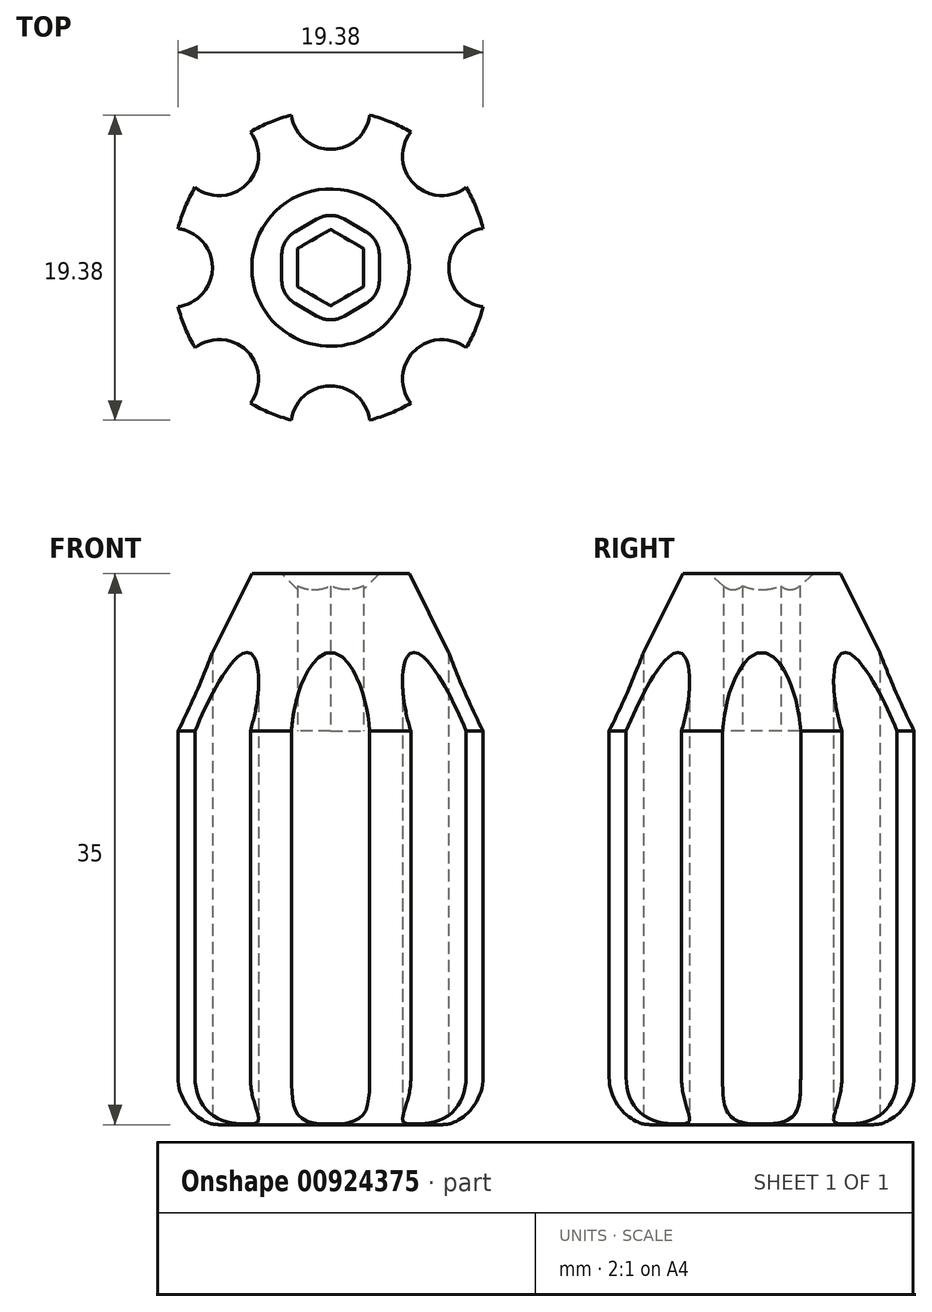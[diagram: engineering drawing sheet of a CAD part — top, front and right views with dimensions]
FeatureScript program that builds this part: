
annotation { "Feature Type Name" : "Feature", "Feature Type Description" : "" }
export const myFeature = defineFeature(function(context is Context, id is Id, definition is map)
    precondition{}
    {
        {
            var Q0;
            Q0=qCreatedBy(makeId("Top.planeOp"),FACE);
            var sketch = newSketch(context, id + "F0", { "sketchPlane" : qUnion([Q0])});
            skCircle(sketch, "E0", {"center": v(0, 0) * mm, "radius": 10 * mm});
            skCircle(sketch, "E1.cCircle", {"center": v(0, 0) * mm, "radius": 2.1 * mm, "construction": true});
            skLineSegment(sketch, "E1.0", {"start": v(2.1, 1.21) * mm, "end": v(2.1, -1.21) * mm});
            skLineSegment(sketch, "E1.1", {"start": v(2.1, -1.21) * mm, "end": v(0, -2.42) * mm});
            skLineSegment(sketch, "E1.2", {"start": v(0, -2.42) * mm, "end": v(-2.1, -1.21) * mm});
            skLineSegment(sketch, "E1.3", {"start": v(-2.1, -1.21) * mm, "end": v(-2.1, 1.21) * mm});
            skLineSegment(sketch, "E1.4", {"start": v(-2.1, 1.21) * mm, "end": v(0, 2.42) * mm});
            skLineSegment(sketch, "E1.5", {"start": v(0, 2.42) * mm, "end": v(2.1, 1.21) * mm});
            skPoint(sketch, "E1.0.midPoint", {"position": v(2.1, 0) * mm});
            skCircle(sketch, "E2", {"center": v(0, 10) * mm, "radius": 2.5 * mm});
            skCircle(sketch, "E3.1.0", {"center": v(-7.07, 7.07) * mm, "radius": 2.5 * mm});
            skCircle(sketch, "E3.2.0", {"center": v(-10, 0) * mm, "radius": 2.5 * mm});
            skCircle(sketch, "E3.3.0", {"center": v(-7.07, -7.07) * mm, "radius": 2.5 * mm});
            skCircle(sketch, "E3.4.0", {"center": v(0, -10) * mm, "radius": 2.5 * mm});
            skCircle(sketch, "E3.5.0", {"center": v(7.07, -7.07) * mm, "radius": 2.5 * mm});
            skCircle(sketch, "E3.6.0", {"center": v(10, 0) * mm, "radius": 2.5 * mm});
            skCircle(sketch, "E3.7.0", {"center": v(7.07, 7.07) * mm, "radius": 2.5 * mm});
            skSolve(sketch);
        }
        {
            var Q0;
            {var subQ6=sQuery(id+"F0.wireOp",EDGE,"E0");var subQ9=sQuery(id+"F0.wireOp",EDGE,"E3.1.0");var subQ10=makeQuery(id+"F0.imprint","INTERSECT",VERTEX,{"disambiguationData":[OD(1.0)],"derivedFrom":[subQ6,subQ9]});Q0=makeQuery(id+"F0.imprint","IMPRINT",FACE,{"disambiguationData":[TD([[makeQuery(id+"F0.imprint","IMPRINT",EDGE,{"disambiguationData":[TD([[subQ10,-1.0]])],"derivedFrom":subQ6}),1.0]])]});}
            var Q1;
            {var subQ0=sQuery(id+"F0.wireOp",EDGE,"Lzq0tQn3-zmQ7-VaXY-TnWL-NvxHLgQxm2Bj");var subQ1=sQuery(id+"F0.wireOp",EDGE,"DYPGsvN2-RAWE-5xOr-ueOZ-kodBmIYwBUKR");var subQ2=makeQuery(id+"F0.imprint","INTERSECT",VERTEX,{"disambiguationData":[OD(0.0)],"derivedFrom":[subQ1,subQ0]});Q1=makeQuery(id+"F0.imprint","IMPRINT",FACE,{"disambiguationData":[TD([[makeQuery(id+"F0.imprint","IMPRINT",EDGE,{"disambiguationData":[TD([[subQ2,-1.0]])],"derivedFrom":subQ1}),1.0]])]});}
            var Q2;
            {var subQ1=sQuery(id+"F0.wireOp",EDGE,"E0");var subQ12=sQuery(id+"F0.wireOp",EDGE,"E3.11.0");var subQ13=makeQuery(id+"F0.imprint","INTERSECT",VERTEX,{"disambiguationData":[OD(1.0)],"derivedFrom":[subQ1,subQ12]});Q2=makeQuery(id+"F0.imprint","IMPRINT",FACE,{"disambiguationData":[TD([[makeQuery(id+"F0.imprint","IMPRINT",EDGE,{"disambiguationData":[TD([[subQ13,-1.0]])],"derivedFrom":subQ1}),1.0]])]});}
            var Q3;
            {var subQ5=sQuery(id+"F0.wireOp",EDGE,"E3.10.0");var subQ6=sQuery(id+"F0.wireOp",EDGE,"E0");var subQ7=makeQuery(id+"F0.imprint","INTERSECT",VERTEX,{"disambiguationData":[OD(1.0)],"derivedFrom":[subQ6,subQ5]});Q3=makeQuery(id+"F0.imprint","IMPRINT",FACE,{"disambiguationData":[TD([[makeQuery(id+"F0.imprint","IMPRINT",EDGE,{"disambiguationData":[TD([[subQ7,-1.0]])],"derivedFrom":subQ6}),1.0]])]});}
            var Q4;
            {var subQ1=sQuery(id+"F0.wireOp",EDGE,"E0");var subQ8=sQuery(id+"F0.wireOp",EDGE,"E3.10.0");var subQ9=makeQuery(id+"F0.imprint","INTERSECT",VERTEX,{"disambiguationData":[OD(0.0)],"derivedFrom":[subQ1,subQ8]});Q4=makeQuery(id+"F0.imprint","IMPRINT",FACE,{"disambiguationData":[TD([[makeQuery(id+"F0.imprint","IMPRINT",EDGE,{"disambiguationData":[TD([[subQ9,1.0]])],"derivedFrom":subQ1}),1.0]])]});}
            var Q5;
            {var subQ0=sQuery(id+"F0.wireOp",EDGE,"iq5nXlA1-twKB-VV0K-wLbr-YbvAK5noPxXK");var subQ1=sQuery(id+"F0.wireOp",EDGE,"E0");var subQ2=makeQuery(id+"F0.imprint","INTERSECT",VERTEX,{"disambiguationData":[OD(1.0)],"derivedFrom":[subQ1,subQ0]});Q5=makeQuery(id+"F0.imprint","IMPRINT",FACE,{"disambiguationData":[TD([[makeQuery(id+"F0.imprint","IMPRINT",EDGE,{"disambiguationData":[TD([[subQ2,-1.0]])],"derivedFrom":subQ1}),1.0]])]});}
            var Q6;
            {var subQ0=sQuery(id+"F0.wireOp",EDGE,"iq5nXlA1-twKB-VV0K-wLbr-YbvAK5noPxXK");var subQ1=sQuery(id+"F0.wireOp",EDGE,"E0");var subQ2=makeQuery(id+"F0.imprint","INTERSECT",VERTEX,{"disambiguationData":[OD(1.0)],"derivedFrom":[subQ1,subQ0]});Q6=makeQuery(id+"F0.imprint","IMPRINT",FACE,{"disambiguationData":[TD([[makeQuery(id+"F0.imprint","IMPRINT",EDGE,{"disambiguationData":[TD([[subQ2,1.0]])],"derivedFrom":subQ1}),1.0]])]});}
            var Q7;
            {var subQ0=sQuery(id+"F0.wireOp",EDGE,"LrOnNZfW-nTIl-rACn-o9rB-nAGoXEMnr8V9");var subQ1=sQuery(id+"F0.wireOp",EDGE,"E0");var subQ2=makeQuery(id+"F0.imprint","INTERSECT",VERTEX,{"disambiguationData":[OD(0.0)],"derivedFrom":[subQ1,subQ0]});Q7=makeQuery(id+"F0.imprint","IMPRINT",FACE,{"disambiguationData":[TD([[makeQuery(id+"F0.imprint","IMPRINT",EDGE,{"disambiguationData":[TD([[subQ2,1.0]])],"derivedFrom":subQ1}),1.0]])]});}
            var Q8;
            {var subQ0=sQuery(id+"F0.wireOp",EDGE,"Lzq0tQn3-zmQ7-VaXY-TnWL-NvxHLgQxm2Bj");var subQ1=sQuery(id+"F0.wireOp",EDGE,"E0");var subQ2=makeQuery(id+"F0.imprint","INTERSECT",VERTEX,{"disambiguationData":[OD(1.0)],"derivedFrom":[subQ1,subQ0]});Q8=makeQuery(id+"F0.imprint","IMPRINT",FACE,{"disambiguationData":[TD([[makeQuery(id+"F0.imprint","IMPRINT",EDGE,{"disambiguationData":[TD([[subQ2,-1.0]])],"derivedFrom":subQ1}),1.0]])]});}
            var Q9;
            {var subQ0=sQuery(id+"F0.wireOp",EDGE,"Lzq0tQn3-zmQ7-VaXY-TnWL-NvxHLgQxm2Bj");var subQ1=sQuery(id+"F0.wireOp",EDGE,"E0");var subQ2=makeQuery(id+"F0.imprint","INTERSECT",VERTEX,{"disambiguationData":[OD(1.0)],"derivedFrom":[subQ1,subQ0]});Q9=makeQuery(id+"F0.imprint","IMPRINT",FACE,{"disambiguationData":[TD([[makeQuery(id+"F0.imprint","IMPRINT",EDGE,{"disambiguationData":[TD([[subQ2,1.0]])],"derivedFrom":subQ1}),1.0]])]});}
            var Q10;
            {var subQ1=sQuery(id+"F0.wireOp",EDGE,"E0");var subQ5=sQuery(id+"F0.wireOp",EDGE,"E3.7.0");var subQ6=makeQuery(id+"F0.imprint","INTERSECT",VERTEX,{"disambiguationData":[OD(1.0)],"derivedFrom":[subQ1,subQ5]});Q10=makeQuery(id+"F0.imprint","IMPRINT",FACE,{"disambiguationData":[TD([[makeQuery(id+"F0.imprint","IMPRINT",EDGE,{"disambiguationData":[TD([[subQ6,-1.0]])],"derivedFrom":subQ1}),1.0]])]});}
            var Q11;
            {var subQ0=sQuery(id+"F0.wireOp",EDGE,"E3.9.0");var subQ1=sQuery(id+"F0.wireOp",EDGE,"E0");var subQ2=makeQuery(id+"F0.imprint","INTERSECT",VERTEX,{"disambiguationData":[OD(0.0)],"derivedFrom":[subQ1,subQ0]});Q11=makeQuery(id+"F0.imprint","IMPRINT",FACE,{"disambiguationData":[TD([[makeQuery(id+"F0.imprint","IMPRINT",EDGE,{"disambiguationData":[TD([[subQ2,1.0]])],"derivedFrom":subQ1}),1.0]])]});}
            var Q12;
            {var subQ0=sQuery(id+"F0.wireOp",EDGE,"E3.5.0");var subQ1=sQuery(id+"F0.wireOp",EDGE,"E0");var subQ2=makeQuery(id+"F0.imprint","INTERSECT",VERTEX,{"disambiguationData":[OD(1.0)],"derivedFrom":[subQ1,subQ0]});Q12=makeQuery(id+"F0.imprint","IMPRINT",FACE,{"disambiguationData":[TD([[makeQuery(id+"F0.imprint","IMPRINT",EDGE,{"disambiguationData":[TD([[subQ2,-1.0]])],"derivedFrom":subQ1}),1.0]])]});}
            var Q13;
            {var subQ0=sQuery(id+"F0.wireOp",EDGE,"E3.6.0");var subQ1=sQuery(id+"F0.wireOp",EDGE,"E0");var subQ2=makeQuery(id+"F0.imprint","INTERSECT",VERTEX,{"disambiguationData":[OD(0.0)],"derivedFrom":[subQ1,subQ0]});Q13=makeQuery(id+"F0.imprint","IMPRINT",FACE,{"disambiguationData":[TD([[makeQuery(id+"F0.imprint","IMPRINT",EDGE,{"disambiguationData":[TD([[subQ2,-1.0]])],"derivedFrom":subQ1}),1.0]])]});}
            var Q14;
            {var subQ0=sQuery(id+"F0.wireOp",EDGE,"DaHCeAtm-5SFQ-LGW9-yzzW-rRFCzOuSfmrK");var subQ1=sQuery(id+"F0.wireOp",EDGE,"E0");var subQ2=makeQuery(id+"F0.imprint","INTERSECT",VERTEX,{"disambiguationData":[OD(0.0)],"derivedFrom":[subQ1,subQ0]});Q14=makeQuery(id+"F0.imprint","IMPRINT",FACE,{"disambiguationData":[TD([[makeQuery(id+"F0.imprint","IMPRINT",EDGE,{"disambiguationData":[TD([[subQ2,-1.0]])],"derivedFrom":subQ1}),1.0]])]});}
            var Q15;
            {var subQ0=sQuery(id+"F0.wireOp",EDGE,"DaHCeAtm-5SFQ-LGW9-yzzW-rRFCzOuSfmrK");var subQ1=sQuery(id+"F0.wireOp",EDGE,"E0");var subQ2=makeQuery(id+"F0.imprint","INTERSECT",VERTEX,{"disambiguationData":[OD(0.0)],"derivedFrom":[subQ1,subQ0]});Q15=makeQuery(id+"F0.imprint","IMPRINT",FACE,{"disambiguationData":[TD([[makeQuery(id+"F0.imprint","IMPRINT",EDGE,{"disambiguationData":[TD([[subQ2,1.0]])],"derivedFrom":subQ1}),1.0]])]});}
            var Q16;
            {var subQ1=sQuery(id+"F0.wireOp",EDGE,"E0");var subQ9=sQuery(id+"F0.wireOp",EDGE,"E3.4.0");var subQ10=makeQuery(id+"F0.imprint","INTERSECT",VERTEX,{"disambiguationData":[OD(1.0)],"derivedFrom":[subQ1,subQ9]});Q16=makeQuery(id+"F0.imprint","IMPRINT",FACE,{"disambiguationData":[TD([[makeQuery(id+"F0.imprint","IMPRINT",EDGE,{"disambiguationData":[TD([[subQ10,-1.0]])],"derivedFrom":subQ1}),1.0]])]});}
            var Q17;
            {var subQ0=sQuery(id+"F0.wireOp",EDGE,"LrOnNZfW-nTIl-rACn-o9rB-nAGoXEMnr8V9");var subQ1=sQuery(id+"F0.wireOp",EDGE,"E0");var subQ2=makeQuery(id+"F0.imprint","INTERSECT",VERTEX,{"disambiguationData":[OD(1.0)],"derivedFrom":[subQ1,subQ0]});Q17=makeQuery(id+"F0.imprint","IMPRINT",FACE,{"disambiguationData":[TD([[makeQuery(id+"F0.imprint","IMPRINT",EDGE,{"disambiguationData":[TD([[subQ2,-1.0]])],"derivedFrom":subQ1}),1.0]])]});}
            var Q18;
            {var subQ0=sQuery(id+"F0.wireOp",EDGE,"LrOnNZfW-nTIl-rACn-o9rB-nAGoXEMnr8V9");var subQ1=sQuery(id+"F0.wireOp",EDGE,"E0");var subQ2=makeQuery(id+"F0.imprint","INTERSECT",VERTEX,{"disambiguationData":[OD(1.0)],"derivedFrom":[subQ1,subQ0]});Q18=makeQuery(id+"F0.imprint","IMPRINT",FACE,{"disambiguationData":[TD([[makeQuery(id+"F0.imprint","IMPRINT",EDGE,{"disambiguationData":[TD([[subQ2,1.0]])],"derivedFrom":subQ1}),1.0]])]});}
            var Q19;
            {var subQ0=sQuery(id+"F0.wireOp",EDGE,"E3.2.0");var subQ1=sQuery(id+"F0.wireOp",EDGE,"E0");var subQ2=makeQuery(id+"F0.imprint","INTERSECT",VERTEX,{"disambiguationData":[OD(1.0)],"derivedFrom":[subQ1,subQ0]});Q19=makeQuery(id+"F0.imprint","IMPRINT",FACE,{"disambiguationData":[TD([[makeQuery(id+"F0.imprint","IMPRINT",EDGE,{"disambiguationData":[TD([[subQ2,-1.0]])],"derivedFrom":subQ1}),1.0]])]});}
            var Q20;
            {var subQ0=sQuery(id+"F0.wireOp",EDGE,"iq5nXlA1-twKB-VV0K-wLbr-YbvAK5noPxXK");var subQ1=sQuery(id+"F0.wireOp",EDGE,"E0");var subQ2=makeQuery(id+"F0.imprint","INTERSECT",VERTEX,{"disambiguationData":[OD(0.0)],"derivedFrom":[subQ1,subQ0]});Q20=makeQuery(id+"F0.imprint","IMPRINT",FACE,{"disambiguationData":[TD([[makeQuery(id+"F0.imprint","IMPRINT",EDGE,{"disambiguationData":[TD([[subQ2,-1.0]])],"derivedFrom":subQ1}),1.0]])]});}
            var Q21;
            {var subQ0=sQuery(id+"F0.wireOp",EDGE,"iq5nXlA1-twKB-VV0K-wLbr-YbvAK5noPxXK");var subQ1=sQuery(id+"F0.wireOp",EDGE,"E0");var subQ2=makeQuery(id+"F0.imprint","INTERSECT",VERTEX,{"disambiguationData":[OD(0.0)],"derivedFrom":[subQ1,subQ0]});Q21=makeQuery(id+"F0.imprint","IMPRINT",FACE,{"disambiguationData":[TD([[makeQuery(id+"F0.imprint","IMPRINT",EDGE,{"disambiguationData":[TD([[subQ2,1.0]])],"derivedFrom":subQ1}),1.0]])]});}
            var Q22;
            {var subQ0=sQuery(id+"F0.wireOp",EDGE,"E2");var subQ1=sQuery(id+"F0.wireOp",EDGE,"E0");var subQ2=makeQuery(id+"F0.imprint","INTERSECT",VERTEX,{"disambiguationData":[OD(0.0)],"derivedFrom":[subQ1,subQ0]});Q22=makeQuery(id+"F0.imprint","IMPRINT",FACE,{"disambiguationData":[TD([[makeQuery(id+"F0.imprint","IMPRINT",EDGE,{"disambiguationData":[TD([[subQ2,-1.0]])],"derivedFrom":subQ1}),1.0]])]});}
            var Q23;
            {var subQ0=sQuery(id+"F0.wireOp",EDGE,"Lzq0tQn3-zmQ7-VaXY-TnWL-NvxHLgQxm2Bj");var subQ1=sQuery(id+"F0.wireOp",EDGE,"E0");var subQ2=makeQuery(id+"F0.imprint","INTERSECT",VERTEX,{"disambiguationData":[OD(0.0)],"derivedFrom":[subQ1,subQ0]});Q23=makeQuery(id+"F0.imprint","IMPRINT",FACE,{"disambiguationData":[TD([[makeQuery(id+"F0.imprint","IMPRINT",EDGE,{"disambiguationData":[TD([[subQ2,-1.0]])],"derivedFrom":subQ1}),1.0]])]});}
            var Q24;
            {var subQ0=sQuery(id+"F0.wireOp",EDGE,"Lzq0tQn3-zmQ7-VaXY-TnWL-NvxHLgQxm2Bj");var subQ1=sQuery(id+"F0.wireOp",EDGE,"E0");var subQ2=makeQuery(id+"F0.imprint","INTERSECT",VERTEX,{"disambiguationData":[OD(0.0)],"derivedFrom":[subQ1,subQ0]});Q24=makeQuery(id+"F0.imprint","IMPRINT",FACE,{"disambiguationData":[TD([[makeQuery(id+"F0.imprint","IMPRINT",EDGE,{"disambiguationData":[TD([[subQ2,1.0]])],"derivedFrom":subQ1}),1.0]])]});}
            var Q25;
            {var subQ0=sQuery(id+"F0.wireOp",EDGE,"LrOnNZfW-nTIl-rACn-o9rB-nAGoXEMnr8V9");var subQ1=sQuery(id+"F0.wireOp",EDGE,"E0");var subQ2=makeQuery(id+"F0.imprint","INTERSECT",VERTEX,{"disambiguationData":[OD(0.0)],"derivedFrom":[subQ1,subQ0]});Q25=makeQuery(id+"F0.imprint","IMPRINT",FACE,{"disambiguationData":[TD([[makeQuery(id+"F0.imprint","IMPRINT",EDGE,{"disambiguationData":[TD([[subQ2,-1.0]])],"derivedFrom":subQ1}),1.0]])]});}
            var Q26;
            {var subQ0=sQuery(id+"F0.wireOp",EDGE,"DaHCeAtm-5SFQ-LGW9-yzzW-rRFCzOuSfmrK");var subQ1=sQuery(id+"F0.wireOp",EDGE,"E0");var subQ2=makeQuery(id+"F0.imprint","INTERSECT",VERTEX,{"disambiguationData":[OD(1.0)],"derivedFrom":[subQ1,subQ0]});Q26=makeQuery(id+"F0.imprint","IMPRINT",FACE,{"disambiguationData":[TD([[makeQuery(id+"F0.imprint","IMPRINT",EDGE,{"disambiguationData":[TD([[subQ2,1.0]])],"derivedFrom":subQ1}),1.0]])]});}
            var Q27;
            {var subQ0=sQuery(id+"F0.wireOp",EDGE,"DaHCeAtm-5SFQ-LGW9-yzzW-rRFCzOuSfmrK");var subQ1=sQuery(id+"F0.wireOp",EDGE,"E0");var subQ2=makeQuery(id+"F0.imprint","INTERSECT",VERTEX,{"disambiguationData":[OD(1.0)],"derivedFrom":[subQ1,subQ0]});Q27=makeQuery(id+"F0.imprint","IMPRINT",FACE,{"disambiguationData":[TD([[makeQuery(id+"F0.imprint","IMPRINT",EDGE,{"disambiguationData":[TD([[subQ2,-1.0]])],"derivedFrom":subQ1}),1.0]])]});}
            var Q28;
            {var subQ0=sQuery(id+"F0.wireOp",EDGE,"DaHCeAtm-5SFQ-LGW9-yzzW-rRFCzOuSfmrK");var subQ1=sQuery(id+"F0.wireOp",EDGE,"DYPGsvN2-RAWE-5xOr-ueOZ-kodBmIYwBUKR");var subQ2=makeQuery(id+"F0.imprint","INTERSECT",VERTEX,{"disambiguationData":[OD(1.0)],"derivedFrom":[subQ1,subQ0]});Q28=makeQuery(id+"F0.imprint","IMPRINT",FACE,{"disambiguationData":[TD([[makeQuery(id+"F0.imprint","IMPRINT",EDGE,{"disambiguationData":[TD([[subQ2,-1.0]])],"derivedFrom":subQ1}),1.0]])]});}
            var Q29;
            {var subQ0=sQuery(id+"F0.wireOp",EDGE,"iq5nXlA1-twKB-VV0K-wLbr-YbvAK5noPxXK");var subQ1=sQuery(id+"F0.wireOp",EDGE,"DYPGsvN2-RAWE-5xOr-ueOZ-kodBmIYwBUKR");var subQ2=makeQuery(id+"F0.imprint","INTERSECT",VERTEX,{"disambiguationData":[OD(1.0)],"derivedFrom":[subQ1,subQ0]});Q29=makeQuery(id+"F0.imprint","IMPRINT",FACE,{"disambiguationData":[TD([[makeQuery(id+"F0.imprint","IMPRINT",EDGE,{"disambiguationData":[TD([[subQ2,-1.0]])],"derivedFrom":subQ1}),1.0]])]});}
            var Q30;
            Q30=makeQuery(id+"F0.imprint","IMPRINT",FACE,{"disambiguationData":[TD([[makeQuery(id+"F0.imprint","IMPRINT",EDGE,{"derivedFrom":sQuery(id+"F0.wireOp",EDGE,"E1.0")}),1.0]])]});
            var Q31;
            {var subQ0=sQuery(id+"F0.wireOp",EDGE,"iq5nXlA1-twKB-VV0K-wLbr-YbvAK5noPxXK");var subQ1=sQuery(id+"F0.wireOp",EDGE,"DYPGsvN2-RAWE-5xOr-ueOZ-kodBmIYwBUKR");var subQ2=makeQuery(id+"F0.imprint","INTERSECT",VERTEX,{"disambiguationData":[OD(0.0)],"derivedFrom":[subQ1,subQ0]});Q31=makeQuery(id+"F0.imprint","IMPRINT",FACE,{"disambiguationData":[TD([[makeQuery(id+"F0.imprint","IMPRINT",EDGE,{"disambiguationData":[TD([[subQ2,1.0]])],"derivedFrom":subQ1}),1.0]])]});}
            var Q32;
            {var subQ0=sQuery(id+"F0.wireOp",EDGE,"E3.3.0");var subQ1=sQuery(id+"F0.wireOp",EDGE,"E0");var subQ2=makeQuery(id+"F0.imprint","INTERSECT",VERTEX,{"disambiguationData":[OD(0.0)],"derivedFrom":[subQ1,subQ0]});Q32=makeQuery(id+"F0.imprint","IMPRINT",FACE,{"disambiguationData":[TD([[makeQuery(id+"F0.imprint","IMPRINT",EDGE,{"disambiguationData":[TD([[subQ2,-1.0]])],"derivedFrom":subQ1}),1.0]])]});}
            var Q33;
            {var subQ0=sQuery(id+"F0.wireOp",EDGE,"E3.2.0");var subQ1=sQuery(id+"F0.wireOp",EDGE,"E0");var subQ2=makeQuery(id+"F0.imprint","INTERSECT",VERTEX,{"disambiguationData":[OD(0.0)],"derivedFrom":[subQ1,subQ0]});Q33=makeQuery(id+"F0.imprint","IMPRINT",FACE,{"disambiguationData":[TD([[makeQuery(id+"F0.imprint","IMPRINT",EDGE,{"disambiguationData":[TD([[subQ2,-1.0]])],"derivedFrom":subQ1}),1.0]])]});}
            var Q34;
            {var subQ0=sQuery(id+"F0.wireOp",EDGE,"E3.4.0");var subQ1=sQuery(id+"F0.wireOp",EDGE,"E0");var subQ2=makeQuery(id+"F0.imprint","INTERSECT",VERTEX,{"disambiguationData":[OD(0.0)],"derivedFrom":[subQ1,subQ0]});Q34=makeQuery(id+"F0.imprint","IMPRINT",FACE,{"disambiguationData":[TD([[makeQuery(id+"F0.imprint","IMPRINT",EDGE,{"disambiguationData":[TD([[subQ2,-1.0]])],"derivedFrom":subQ1}),1.0]])]});}
            var Q35;
            {var subQ0=sQuery(id+"F0.wireOp",EDGE,"E3.5.0");var subQ1=sQuery(id+"F0.wireOp",EDGE,"E0");var subQ2=makeQuery(id+"F0.imprint","INTERSECT",VERTEX,{"disambiguationData":[OD(0.0)],"derivedFrom":[subQ1,subQ0]});Q35=makeQuery(id+"F0.imprint","IMPRINT",FACE,{"disambiguationData":[TD([[makeQuery(id+"F0.imprint","IMPRINT",EDGE,{"disambiguationData":[TD([[subQ2,-1.0]])],"derivedFrom":subQ1}),1.0]])]});}
            var Q36;
            {var subQ0=sQuery(id+"F0.wireOp",EDGE,"E3.6.0");var subQ1=sQuery(id+"F0.wireOp",EDGE,"E0");var subQ2=makeQuery(id+"F0.imprint","INTERSECT",VERTEX,{"disambiguationData":[OD(0.0)],"derivedFrom":[subQ1,subQ0]});Q36=makeQuery(id+"F0.imprint","IMPRINT",FACE,{"disambiguationData":[TD([[makeQuery(id+"F0.imprint","IMPRINT",EDGE,{"disambiguationData":[TD([[subQ2,1.0]])],"derivedFrom":subQ1}),1.0]])]});}
            var Q37;
            {var subQ0=sQuery(id+"F0.wireOp",EDGE,"E3.7.0");var subQ1=sQuery(id+"F0.wireOp",EDGE,"E0");var subQ2=makeQuery(id+"F0.imprint","INTERSECT",VERTEX,{"disambiguationData":[OD(0.0)],"derivedFrom":[subQ1,subQ0]});Q37=makeQuery(id+"F0.imprint","IMPRINT",FACE,{"disambiguationData":[TD([[makeQuery(id+"F0.imprint","IMPRINT",EDGE,{"disambiguationData":[TD([[subQ2,-1.0]])],"derivedFrom":subQ1}),1.0]])]});}
            var Q38;
            {var subQ0=sQuery(id+"F0.wireOp",EDGE,"E3.1.0");var subQ1=sQuery(id+"F0.wireOp",EDGE,"E0");var subQ2=makeQuery(id+"F0.imprint","INTERSECT",VERTEX,{"disambiguationData":[OD(0.0)],"derivedFrom":[subQ1,subQ0]});Q38=makeQuery(id+"F0.imprint","IMPRINT",FACE,{"disambiguationData":[TD([[makeQuery(id+"F0.imprint","IMPRINT",EDGE,{"disambiguationData":[TD([[subQ2,-1.0]])],"derivedFrom":subQ1}),1.0]])]});}
            extrude(context, id + "F1", {"entities" : qUnion([Q0, Q1, Q2, Q3, Q4, Q5, Q6, Q7, Q8, Q9, Q10, Q11, Q12, Q13, Q14, Q15, Q16, Q17, Q18, Q19, Q20, Q21, Q22, Q23, Q24, Q25, Q26, Q27, Q28, Q29, Q30, Q31, Q32, Q33, Q34, Q35, Q36, Q37, Q38]), "depth" : 35 * mm, "offsetDistance" : 25 * mm});
        }
        {
            var Q0;
            Q0=makeQuery(id+"F0.imprint","IMPRINT",FACE,{"disambiguationData":[TD([[makeQuery(id+"F0.imprint","IMPRINT",EDGE,{"derivedFrom":sQuery(id+"F0.wireOp",EDGE,"E1.0")}),-1.0]])]});
            extrude(context, id + "F2", {"entities" : qUnion([Q0]), "operationType" : NewBodyOperationType.ADD, "depth" : 25 * mm, "offsetDistance" : 25 * mm});
        }
        {
            var Q0;
            {var subQ0=sQuery(id+"F0.wireOp",EDGE,"E3.1.0");var subQ1=sQuery(id+"F0.wireOp",EDGE,"E0");Q0=makeQuery(id+"F7.boolean.opBoolean","COPY",EDGE,{"derivedFrom":makeQuery(id+"F7.opExtrude","SWEPT_EDGE",EDGE,{"disambiguationData":[OSD([subQ1,subQ0]),TDD([makeQuery(id+"F0.imprint","INTERSECT",VERTEX,{"disambiguationData":[OD(1.0)],"derivedFrom":[subQ1,subQ0]})])]})});}
            var Q1;
            Q1=makeQuery(id+"F1.opExtrude","CAP_EDGE",EDGE,{"disambiguationData":[OSD([sQuery(id+"F0.wireOp",EDGE,"E0")])],"isStart":true});
            fillet(context, id + "F3", {"entities" : qUnion([Q0, Q1]), "radius" : 3 * mm, "tangentPropagation" : true, "allowEdgeOverflow" : false});
        }
        {
            var Q0;
            Q0=makeQuery(id+"F7.boolean.opBoolean","INTERSECT",EDGE,{"derivedFrom":[makeQuery(id+"F1.opExtrude","CAP_FACE",FACE,{"disambiguationData":[OSD([sQuery(id+"F0.wireOp",EDGE,"E0"),sQuery(id+"F0.wireOp",EDGE,"E1.0"),sQuery(id+"F0.wireOp",EDGE,"E1.1"),sQuery(id+"F0.wireOp",EDGE,"E1.2"),sQuery(id+"F0.wireOp",EDGE,"E1.3"),sQuery(id+"F0.wireOp",EDGE,"E1.4"),sQuery(id+"F0.wireOp",EDGE,"E1.5")])],"isStart":false}),makeQuery(id+"F7.opExtrude","SWEPT_FACE",FACE,{"disambiguationData":[OSD([sQuery(id+"F0.wireOp",EDGE,"E3.1.0")])]})]});
            var Q1;
            Q1=makeQuery(id+"F1.opExtrude","CAP_EDGE",EDGE,{"disambiguationData":[OSD([sQuery(id+"F0.wireOp",EDGE,"E0")])],"isStart":false});
            chamfer(context, id + "F4", {"entities" : qUnion([Q0, Q1]), "chamferType" : ChamferType.TWO_OFFSETS, "width1" : 5 * mm, "oppositeDirection" : false, "width2" : 10 * mm, "tangentPropagation" : true});
        }
        {
            var Q0;
            Q0=makeQuery(id+"F1.opExtrude","CAP_EDGE",EDGE,{"disambiguationData":[OSD([sQuery(id+"F0.wireOp",EDGE,"E1.1")])],"isStart":false});
            var Q1;
            Q1=makeQuery(id+"F1.opExtrude","CAP_EDGE",EDGE,{"disambiguationData":[OSD([sQuery(id+"F0.wireOp",EDGE,"E1.0")])],"isStart":false});
            var Q2;
            Q2=makeQuery(id+"F1.opExtrude","CAP_EDGE",EDGE,{"disambiguationData":[OSD([sQuery(id+"F0.wireOp",EDGE,"E1.5")])],"isStart":false});
            var Q3;
            Q3=makeQuery(id+"F1.opExtrude","CAP_EDGE",EDGE,{"disambiguationData":[OSD([sQuery(id+"F0.wireOp",EDGE,"E1.4")])],"isStart":false});
            var Q4;
            Q4=makeQuery(id+"F1.opExtrude","CAP_EDGE",EDGE,{"disambiguationData":[OSD([sQuery(id+"F0.wireOp",EDGE,"E1.3")])],"isStart":false});
            var Q5;
            Q5=makeQuery(id+"F1.opExtrude","CAP_EDGE",EDGE,{"disambiguationData":[OSD([sQuery(id+"F0.wireOp",EDGE,"E1.2")])],"isStart":false});
            chamfer(context, id + "F5", {"entities" : qUnion([Q0, Q1, Q2, Q3, Q4, Q5]), "width" : 1 * mm, "tangentPropagation" : true});
        }
        {
            var Q0;
            Q0=makeQuery(id+"F5.opChamfer","BLEND_EDGE",EDGE,{"blendedFrom":[makeQuery(id+"F1.opExtrude","CAP_EDGE",EDGE,{"disambiguationData":[OSD([sQuery(id+"F0.wireOp",EDGE,"E1.4")])],"isStart":false}),makeQuery(id+"F1.opExtrude","CAP_EDGE",EDGE,{"disambiguationData":[OSD([sQuery(id+"F0.wireOp",EDGE,"E1.5")])],"isStart":false})],"blendedInto":[]});
            var Q1;
            Q1=makeQuery(id+"F5.opChamfer","BLEND_EDGE",EDGE,{"blendedFrom":[makeQuery(id+"F1.opExtrude","CAP_EDGE",EDGE,{"disambiguationData":[OSD([sQuery(id+"F0.wireOp",EDGE,"E1.0")])],"isStart":false}),makeQuery(id+"F1.opExtrude","CAP_EDGE",EDGE,{"disambiguationData":[OSD([sQuery(id+"F0.wireOp",EDGE,"E1.5")])],"isStart":false})],"blendedInto":[]});
            var Q2;
            Q2=makeQuery(id+"F5.opChamfer","BLEND_EDGE",EDGE,{"blendedFrom":[makeQuery(id+"F1.opExtrude","CAP_EDGE",EDGE,{"disambiguationData":[OSD([sQuery(id+"F0.wireOp",EDGE,"E1.0")])],"isStart":false}),makeQuery(id+"F1.opExtrude","CAP_EDGE",EDGE,{"disambiguationData":[OSD([sQuery(id+"F0.wireOp",EDGE,"E1.1")])],"isStart":false})],"blendedInto":[]});
            var Q3;
            Q3=makeQuery(id+"F5.opChamfer","BLEND_EDGE",EDGE,{"blendedFrom":[makeQuery(id+"F1.opExtrude","CAP_EDGE",EDGE,{"disambiguationData":[OSD([sQuery(id+"F0.wireOp",EDGE,"E1.1")])],"isStart":false}),makeQuery(id+"F1.opExtrude","CAP_EDGE",EDGE,{"disambiguationData":[OSD([sQuery(id+"F0.wireOp",EDGE,"E1.2")])],"isStart":false})],"blendedInto":[]});
            var Q4;
            Q4=makeQuery(id+"F5.opChamfer","BLEND_EDGE",EDGE,{"blendedFrom":[makeQuery(id+"F1.opExtrude","CAP_EDGE",EDGE,{"disambiguationData":[OSD([sQuery(id+"F0.wireOp",EDGE,"E1.2")])],"isStart":false}),makeQuery(id+"F1.opExtrude","CAP_EDGE",EDGE,{"disambiguationData":[OSD([sQuery(id+"F0.wireOp",EDGE,"E1.3")])],"isStart":false})],"blendedInto":[]});
            var Q5;
            Q5=makeQuery(id+"F5.opChamfer","BLEND_EDGE",EDGE,{"blendedFrom":[makeQuery(id+"F1.opExtrude","CAP_EDGE",EDGE,{"disambiguationData":[OSD([sQuery(id+"F0.wireOp",EDGE,"E1.3")])],"isStart":false}),makeQuery(id+"F1.opExtrude","CAP_EDGE",EDGE,{"disambiguationData":[OSD([sQuery(id+"F0.wireOp",EDGE,"E1.4")])],"isStart":false})],"blendedInto":[]});
            fillet(context, id + "F6", {"entities" : qUnion([Q0, Q1, Q2, Q3, Q4, Q5]), "radius" : 2.5 * mm, "tangentPropagation" : true, "allowEdgeOverflow" : false});
        }
        {
            var Q0;
            {var subQ0=sQuery(id+"F0.wireOp",EDGE,"LrOnNZfW-nTIl-rACn-o9rB-nAGoXEMnr8V9");var subQ1=sQuery(id+"F0.wireOp",EDGE,"E0");var subQ2=makeQuery(id+"F0.imprint","INTERSECT",VERTEX,{"disambiguationData":[OD(0.0)],"derivedFrom":[subQ1,subQ0]});Q0=makeQuery(id+"F0.imprint","IMPRINT",FACE,{"disambiguationData":[TD([[makeQuery(id+"F0.imprint","IMPRINT",EDGE,{"disambiguationData":[TD([[subQ2,-1.0]])],"derivedFrom":subQ1}),1.0]])]});}
            var Q1;
            {var subQ0=sQuery(id+"F0.wireOp",EDGE,"LrOnNZfW-nTIl-rACn-o9rB-nAGoXEMnr8V9");var subQ1=sQuery(id+"F0.wireOp",EDGE,"E0");var subQ2=makeQuery(id+"F0.imprint","INTERSECT",VERTEX,{"disambiguationData":[OD(0.0)],"derivedFrom":[subQ1,subQ0]});Q1=makeQuery(id+"F0.imprint","IMPRINT",FACE,{"disambiguationData":[TD([[makeQuery(id+"F0.imprint","IMPRINT",EDGE,{"disambiguationData":[TD([[subQ2,1.0]])],"derivedFrom":subQ1}),1.0]])]});}
            var Q2;
            {var subQ0=sQuery(id+"F0.wireOp",EDGE,"Lzq0tQn3-zmQ7-VaXY-TnWL-NvxHLgQxm2Bj");var subQ1=sQuery(id+"F0.wireOp",EDGE,"E0");var subQ2=makeQuery(id+"F0.imprint","INTERSECT",VERTEX,{"disambiguationData":[OD(1.0)],"derivedFrom":[subQ1,subQ0]});Q2=makeQuery(id+"F0.imprint","IMPRINT",FACE,{"disambiguationData":[TD([[makeQuery(id+"F0.imprint","IMPRINT",EDGE,{"disambiguationData":[TD([[subQ2,-1.0]])],"derivedFrom":subQ1}),1.0]])]});}
            var Q3;
            {var subQ0=sQuery(id+"F0.wireOp",EDGE,"Lzq0tQn3-zmQ7-VaXY-TnWL-NvxHLgQxm2Bj");var subQ1=sQuery(id+"F0.wireOp",EDGE,"E0");var subQ2=makeQuery(id+"F0.imprint","INTERSECT",VERTEX,{"disambiguationData":[OD(1.0)],"derivedFrom":[subQ1,subQ0]});Q3=makeQuery(id+"F0.imprint","IMPRINT",FACE,{"disambiguationData":[TD([[makeQuery(id+"F0.imprint","IMPRINT",EDGE,{"disambiguationData":[TD([[subQ2,1.0]])],"derivedFrom":subQ1}),1.0]])]});}
            var Q4;
            {var subQ0=sQuery(id+"F0.wireOp",EDGE,"DaHCeAtm-5SFQ-LGW9-yzzW-rRFCzOuSfmrK");var subQ1=sQuery(id+"F0.wireOp",EDGE,"E0");var subQ2=makeQuery(id+"F0.imprint","INTERSECT",VERTEX,{"disambiguationData":[OD(0.0)],"derivedFrom":[subQ1,subQ0]});Q4=makeQuery(id+"F0.imprint","IMPRINT",FACE,{"disambiguationData":[TD([[makeQuery(id+"F0.imprint","IMPRINT",EDGE,{"disambiguationData":[TD([[subQ2,-1.0]])],"derivedFrom":subQ1}),1.0]])]});}
            var Q5;
            {var subQ0=sQuery(id+"F0.wireOp",EDGE,"DaHCeAtm-5SFQ-LGW9-yzzW-rRFCzOuSfmrK");var subQ1=sQuery(id+"F0.wireOp",EDGE,"E0");var subQ2=makeQuery(id+"F0.imprint","INTERSECT",VERTEX,{"disambiguationData":[OD(0.0)],"derivedFrom":[subQ1,subQ0]});Q5=makeQuery(id+"F0.imprint","IMPRINT",FACE,{"disambiguationData":[TD([[makeQuery(id+"F0.imprint","IMPRINT",EDGE,{"disambiguationData":[TD([[subQ2,1.0]])],"derivedFrom":subQ1}),1.0]])]});}
            var Q6;
            {var subQ0=sQuery(id+"F0.wireOp",EDGE,"LrOnNZfW-nTIl-rACn-o9rB-nAGoXEMnr8V9");var subQ1=sQuery(id+"F0.wireOp",EDGE,"E0");var subQ2=makeQuery(id+"F0.imprint","INTERSECT",VERTEX,{"disambiguationData":[OD(1.0)],"derivedFrom":[subQ1,subQ0]});Q6=makeQuery(id+"F0.imprint","IMPRINT",FACE,{"disambiguationData":[TD([[makeQuery(id+"F0.imprint","IMPRINT",EDGE,{"disambiguationData":[TD([[subQ2,-1.0]])],"derivedFrom":subQ1}),1.0]])]});}
            var Q7;
            {var subQ0=sQuery(id+"F0.wireOp",EDGE,"LrOnNZfW-nTIl-rACn-o9rB-nAGoXEMnr8V9");var subQ1=sQuery(id+"F0.wireOp",EDGE,"E0");var subQ2=makeQuery(id+"F0.imprint","INTERSECT",VERTEX,{"disambiguationData":[OD(1.0)],"derivedFrom":[subQ1,subQ0]});Q7=makeQuery(id+"F0.imprint","IMPRINT",FACE,{"disambiguationData":[TD([[makeQuery(id+"F0.imprint","IMPRINT",EDGE,{"disambiguationData":[TD([[subQ2,1.0]])],"derivedFrom":subQ1}),1.0]])]});}
            var Q8;
            {var subQ0=sQuery(id+"F0.wireOp",EDGE,"E3.3.0");var subQ1=sQuery(id+"F0.wireOp",EDGE,"E0");var subQ2=makeQuery(id+"F0.imprint","INTERSECT",VERTEX,{"disambiguationData":[OD(0.0)],"derivedFrom":[subQ1,subQ0]});Q8=makeQuery(id+"F0.imprint","IMPRINT",FACE,{"disambiguationData":[TD([[makeQuery(id+"F0.imprint","IMPRINT",EDGE,{"disambiguationData":[TD([[subQ2,-1.0]])],"derivedFrom":subQ1}),1.0]])]});}
            var Q9;
            {var subQ0=sQuery(id+"F0.wireOp",EDGE,"iq5nXlA1-twKB-VV0K-wLbr-YbvAK5noPxXK");var subQ1=sQuery(id+"F0.wireOp",EDGE,"E0");var subQ2=makeQuery(id+"F0.imprint","INTERSECT",VERTEX,{"disambiguationData":[OD(0.0)],"derivedFrom":[subQ1,subQ0]});Q9=makeQuery(id+"F0.imprint","IMPRINT",FACE,{"disambiguationData":[TD([[makeQuery(id+"F0.imprint","IMPRINT",EDGE,{"disambiguationData":[TD([[subQ2,-1.0]])],"derivedFrom":subQ1}),1.0]])]});}
            var Q10;
            {var subQ0=sQuery(id+"F0.wireOp",EDGE,"iq5nXlA1-twKB-VV0K-wLbr-YbvAK5noPxXK");var subQ1=sQuery(id+"F0.wireOp",EDGE,"E0");var subQ2=makeQuery(id+"F0.imprint","INTERSECT",VERTEX,{"disambiguationData":[OD(0.0)],"derivedFrom":[subQ1,subQ0]});Q10=makeQuery(id+"F0.imprint","IMPRINT",FACE,{"disambiguationData":[TD([[makeQuery(id+"F0.imprint","IMPRINT",EDGE,{"disambiguationData":[TD([[subQ2,1.0]])],"derivedFrom":subQ1}),1.0]])]});}
            var Q11;
            {var subQ0=sQuery(id+"F0.wireOp",EDGE,"E3.9.0");var subQ1=sQuery(id+"F0.wireOp",EDGE,"E0");var subQ2=makeQuery(id+"F0.imprint","INTERSECT",VERTEX,{"disambiguationData":[OD(0.0)],"derivedFrom":[subQ1,subQ0]});Q11=makeQuery(id+"F0.imprint","IMPRINT",FACE,{"disambiguationData":[TD([[makeQuery(id+"F0.imprint","IMPRINT",EDGE,{"disambiguationData":[TD([[subQ2,1.0]])],"derivedFrom":subQ1}),1.0]])]});}
            var Q12;
            {var subQ0=sQuery(id+"F0.wireOp",EDGE,"iq5nXlA1-twKB-VV0K-wLbr-YbvAK5noPxXK");var subQ1=sQuery(id+"F0.wireOp",EDGE,"E0");var subQ2=makeQuery(id+"F0.imprint","INTERSECT",VERTEX,{"disambiguationData":[OD(1.0)],"derivedFrom":[subQ1,subQ0]});Q12=makeQuery(id+"F0.imprint","IMPRINT",FACE,{"disambiguationData":[TD([[makeQuery(id+"F0.imprint","IMPRINT",EDGE,{"disambiguationData":[TD([[subQ2,1.0]])],"derivedFrom":subQ1}),1.0]])]});}
            var Q13;
            {var subQ0=sQuery(id+"F0.wireOp",EDGE,"iq5nXlA1-twKB-VV0K-wLbr-YbvAK5noPxXK");var subQ1=sQuery(id+"F0.wireOp",EDGE,"E0");var subQ2=makeQuery(id+"F0.imprint","INTERSECT",VERTEX,{"disambiguationData":[OD(1.0)],"derivedFrom":[subQ1,subQ0]});Q13=makeQuery(id+"F0.imprint","IMPRINT",FACE,{"disambiguationData":[TD([[makeQuery(id+"F0.imprint","IMPRINT",EDGE,{"disambiguationData":[TD([[subQ2,-1.0]])],"derivedFrom":subQ1}),1.0]])]});}
            var Q14;
            {var subQ0=sQuery(id+"F0.wireOp",EDGE,"Lzq0tQn3-zmQ7-VaXY-TnWL-NvxHLgQxm2Bj");var subQ1=sQuery(id+"F0.wireOp",EDGE,"E0");var subQ2=makeQuery(id+"F0.imprint","INTERSECT",VERTEX,{"disambiguationData":[OD(0.0)],"derivedFrom":[subQ1,subQ0]});Q14=makeQuery(id+"F0.imprint","IMPRINT",FACE,{"disambiguationData":[TD([[makeQuery(id+"F0.imprint","IMPRINT",EDGE,{"disambiguationData":[TD([[subQ2,1.0]])],"derivedFrom":subQ1}),1.0]])]});}
            var Q15;
            {var subQ0=sQuery(id+"F0.wireOp",EDGE,"Lzq0tQn3-zmQ7-VaXY-TnWL-NvxHLgQxm2Bj");var subQ1=sQuery(id+"F0.wireOp",EDGE,"E0");var subQ2=makeQuery(id+"F0.imprint","INTERSECT",VERTEX,{"disambiguationData":[OD(0.0)],"derivedFrom":[subQ1,subQ0]});Q15=makeQuery(id+"F0.imprint","IMPRINT",FACE,{"disambiguationData":[TD([[makeQuery(id+"F0.imprint","IMPRINT",EDGE,{"disambiguationData":[TD([[subQ2,-1.0]])],"derivedFrom":subQ1}),1.0]])]});}
            var Q16;
            {var subQ0=sQuery(id+"F0.wireOp",EDGE,"E2");var subQ1=sQuery(id+"F0.wireOp",EDGE,"E0");var subQ2=makeQuery(id+"F0.imprint","INTERSECT",VERTEX,{"disambiguationData":[OD(0.0)],"derivedFrom":[subQ1,subQ0]});Q16=makeQuery(id+"F0.imprint","IMPRINT",FACE,{"disambiguationData":[TD([[makeQuery(id+"F0.imprint","IMPRINT",EDGE,{"disambiguationData":[TD([[subQ2,-1.0]])],"derivedFrom":subQ1}),1.0]])]});}
            var Q17;
            {var subQ0=sQuery(id+"F0.wireOp",EDGE,"DaHCeAtm-5SFQ-LGW9-yzzW-rRFCzOuSfmrK");var subQ1=sQuery(id+"F0.wireOp",EDGE,"E0");var subQ2=makeQuery(id+"F0.imprint","INTERSECT",VERTEX,{"disambiguationData":[OD(1.0)],"derivedFrom":[subQ1,subQ0]});Q17=makeQuery(id+"F0.imprint","IMPRINT",FACE,{"disambiguationData":[TD([[makeQuery(id+"F0.imprint","IMPRINT",EDGE,{"disambiguationData":[TD([[subQ2,1.0]])],"derivedFrom":subQ1}),1.0]])]});}
            var Q18;
            {var subQ0=sQuery(id+"F0.wireOp",EDGE,"DaHCeAtm-5SFQ-LGW9-yzzW-rRFCzOuSfmrK");var subQ1=sQuery(id+"F0.wireOp",EDGE,"E0");var subQ2=makeQuery(id+"F0.imprint","INTERSECT",VERTEX,{"disambiguationData":[OD(1.0)],"derivedFrom":[subQ1,subQ0]});Q18=makeQuery(id+"F0.imprint","IMPRINT",FACE,{"disambiguationData":[TD([[makeQuery(id+"F0.imprint","IMPRINT",EDGE,{"disambiguationData":[TD([[subQ2,-1.0]])],"derivedFrom":subQ1}),1.0]])]});}
            var Q19;
            {var subQ0=sQuery(id+"F0.wireOp",EDGE,"E3.1.0");var subQ1=sQuery(id+"F0.wireOp",EDGE,"E0");var subQ2=makeQuery(id+"F0.imprint","INTERSECT",VERTEX,{"disambiguationData":[OD(0.0)],"derivedFrom":[subQ1,subQ0]});Q19=makeQuery(id+"F0.imprint","IMPRINT",FACE,{"disambiguationData":[TD([[makeQuery(id+"F0.imprint","IMPRINT",EDGE,{"disambiguationData":[TD([[subQ2,-1.0]])],"derivedFrom":subQ1}),1.0]])]});}
            var Q20;
            {var subQ0=sQuery(id+"F0.wireOp",EDGE,"E3.2.0");var subQ1=sQuery(id+"F0.wireOp",EDGE,"E0");var subQ2=makeQuery(id+"F0.imprint","INTERSECT",VERTEX,{"disambiguationData":[OD(0.0)],"derivedFrom":[subQ1,subQ0]});Q20=makeQuery(id+"F0.imprint","IMPRINT",FACE,{"disambiguationData":[TD([[makeQuery(id+"F0.imprint","IMPRINT",EDGE,{"disambiguationData":[TD([[subQ2,-1.0]])],"derivedFrom":subQ1}),1.0]])]});}
            var Q21;
            {var subQ0=sQuery(id+"F0.wireOp",EDGE,"E3.4.0");var subQ1=sQuery(id+"F0.wireOp",EDGE,"E0");var subQ2=makeQuery(id+"F0.imprint","INTERSECT",VERTEX,{"disambiguationData":[OD(0.0)],"derivedFrom":[subQ1,subQ0]});Q21=makeQuery(id+"F0.imprint","IMPRINT",FACE,{"disambiguationData":[TD([[makeQuery(id+"F0.imprint","IMPRINT",EDGE,{"disambiguationData":[TD([[subQ2,-1.0]])],"derivedFrom":subQ1}),1.0]])]});}
            var Q22;
            {var subQ0=sQuery(id+"F0.wireOp",EDGE,"E3.5.0");var subQ1=sQuery(id+"F0.wireOp",EDGE,"E0");var subQ2=makeQuery(id+"F0.imprint","INTERSECT",VERTEX,{"disambiguationData":[OD(0.0)],"derivedFrom":[subQ1,subQ0]});Q22=makeQuery(id+"F0.imprint","IMPRINT",FACE,{"disambiguationData":[TD([[makeQuery(id+"F0.imprint","IMPRINT",EDGE,{"disambiguationData":[TD([[subQ2,-1.0]])],"derivedFrom":subQ1}),1.0]])]});}
            var Q23;
            {var subQ0=sQuery(id+"F0.wireOp",EDGE,"E3.6.0");var subQ1=sQuery(id+"F0.wireOp",EDGE,"E0");var subQ2=makeQuery(id+"F0.imprint","INTERSECT",VERTEX,{"disambiguationData":[OD(0.0)],"derivedFrom":[subQ1,subQ0]});Q23=makeQuery(id+"F0.imprint","IMPRINT",FACE,{"disambiguationData":[TD([[makeQuery(id+"F0.imprint","IMPRINT",EDGE,{"disambiguationData":[TD([[subQ2,1.0]])],"derivedFrom":subQ1}),1.0]])]});}
            var Q24;
            {var subQ0=sQuery(id+"F0.wireOp",EDGE,"E3.7.0");var subQ1=sQuery(id+"F0.wireOp",EDGE,"E0");var subQ2=makeQuery(id+"F0.imprint","INTERSECT",VERTEX,{"disambiguationData":[OD(0.0)],"derivedFrom":[subQ1,subQ0]});Q24=makeQuery(id+"F0.imprint","IMPRINT",FACE,{"disambiguationData":[TD([[makeQuery(id+"F0.imprint","IMPRINT",EDGE,{"disambiguationData":[TD([[subQ2,-1.0]])],"derivedFrom":subQ1}),1.0]])]});}
            extrude(context, id + "F7", {"entities" : qUnion([Q0, Q1, Q2, Q3, Q4, Q5, Q6, Q7, Q8, Q9, Q10, Q11, Q12, Q13, Q14, Q15, Q16, Q17, Q18, Q19, Q20, Q21, Q22, Q23, Q24]), "operationType" : NewBodyOperationType.REMOVE, "depth" : 40 * mm, "offsetDistance" : 25 * mm});
        }
    });
